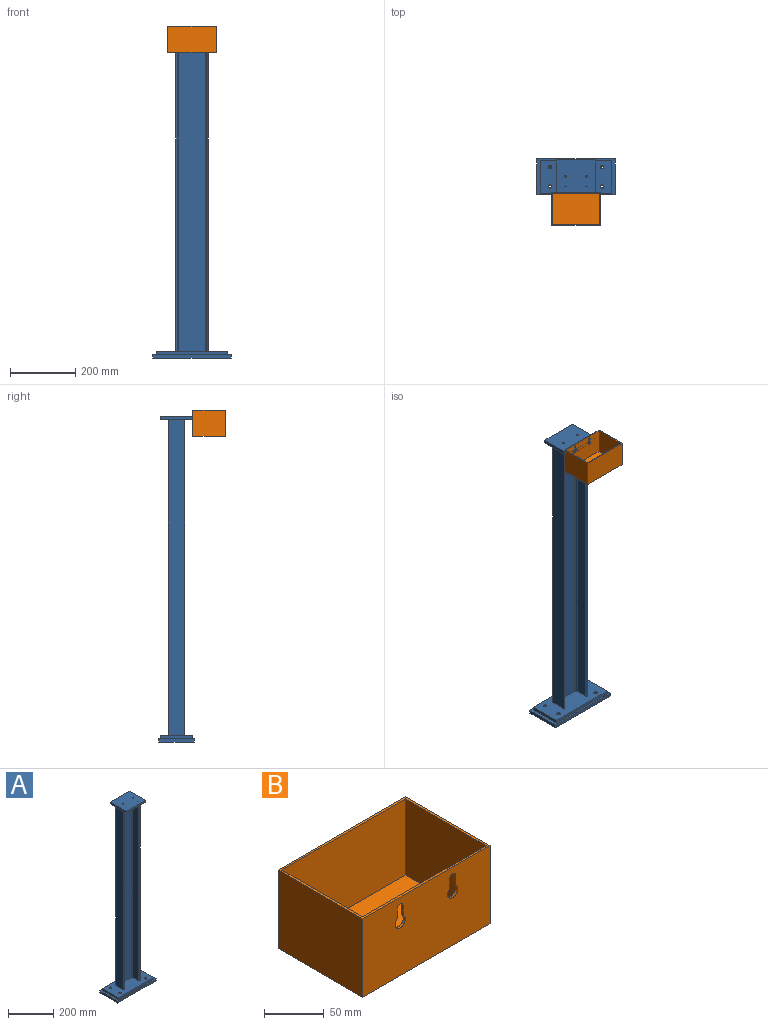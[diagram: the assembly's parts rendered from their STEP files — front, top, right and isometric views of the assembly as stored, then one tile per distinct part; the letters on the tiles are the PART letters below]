
ASSEMBLY  parts=2 mates=1
PART A: 45 faces, bbox 240x110x1000 mm
  f0: plane 220x100mm, normal (0,0,1), area 20669.9mm2, adj f15,f16,f17,f18,f19,f20,f21,f22
  f1: plane 11x11mm, normal (0,0,1), area 44.8mm2, adj f13,f21
  f2: plane 11x11mm, normal (0,0,1), area 44.8mm2, adj f9,f20
  f3: plane 11x11mm, normal (0,0,1), area 44.8mm2, adj f10,f19
  f4: plane 11x11mm, normal (0,0,1), area 44.8mm2, adj f11,f18
  f5: plane 240x110mm, normal (0,0,1), area 4400mm2, adj f6,f7,f8,f12,f15,f16,f17,f22
  f6: plane 110x10mm, normal (1,0,0), area 1100mm2, adj f5,f7,f12,f14
  f7: plane 240x10mm, normal (0,1,0), area 2400mm2, adj f5,f6,f8,f14
  f8: plane 110x10mm, normal (-1,0,0), area 1100mm2, adj f5,f7,f12,f14
  f9: cylinder r=4mm len=10mm, axis (0,0,1), area 251.3mm2, adj f2,f14
  f10: cylinder r=4mm len=10mm, axis (0,0,1), area 251.3mm2, adj f3,f14
  f11: cylinder r=4mm len=10mm, axis (0,0,1), area 251.3mm2, adj f4,f14
  f12: plane 240x10mm, normal (0,-1,0), area 2400mm2, adj f5,f6,f8,f14
  f13: cylinder r=4mm len=10mm, axis (0,0,1), area 251.3mm2, adj f1,f14
  f14: plane 240x110mm, normal (0,0,-1), area 26198.9mm2, adj f6,f7,f8,f9,f10,f11,f12,f13
  f15: plane 220x10mm, normal (0,1,0), area 2200mm2, adj f0,f5,f16,f22
  f16: plane 100x10mm, normal (-1,0,0), area 1000mm2, adj f0,f5,f15,f17
  f17: plane 220x10mm, normal (0,-1,0), area 2200mm2, adj f0,f5,f16,f22
  f18: cylinder r=5.5mm len=11mm, axis (0,0,-1), area 345.6mm2, adj f0,f4
  f19: cylinder r=5.5mm len=11mm, axis (0,0,-1), area 345.6mm2, adj f0,f3
  f20: cylinder r=5.5mm len=11mm, axis (0,0,-1), area 345.6mm2, adj f0,f2
  f21: cylinder r=5.5mm len=11mm, axis (0,0,-1), area 345.6mm2, adj f0,f1
  f22: plane 100x10mm, normal (1,0,0), area 1000mm2, adj f0,f5,f15,f17
  f23: plane 970x50mm, normal (1,0,0), area 48500mm2, adj f0,f24,f32,f33
  f24: plane 970x100mm, normal (0,1,0), area 97000mm2, adj f0,f23,f25,f33
  f25: plane 970x50mm, normal (-1,0,0), area 48500mm2, adj f0,f24,f26,f33
  f26: cylinder r=5mm len=970mm, axis (0,0,-1), area 7618.4mm2, adj f0,f25,f27,f33
  f27: plane 970x35mm, normal (1,0,0), area 33950mm2, adj f0,f26,f28,f33
  f28: cylinder r=5mm len=970mm, axis (0,0,-1), area 7618.4mm2, adj f0,f27,f29,f33
  f29: plane 970x80mm, normal (0,-1,0), area 77600mm2, adj f0,f28,f30,f33
  f30: cylinder r=5mm len=970mm, axis (0,0,-1), area 7618.4mm2, adj f0,f29,f31,f33
  f31: plane 970x35mm, normal (-1,0,0), area 33950mm2, adj f0,f30,f32,f33
  f32: cylinder r=5mm len=970mm, axis (0,0,-1), area 7618.4mm2, adj f0,f23,f31,f33
  f33: plane 120x100mm, normal (0,0,-1), area 10993.5mm2, adj f23,f24,f25,f26,f27,f28,f29,f30
  f34: plane 120x10mm, normal (0,1,0), area 1200mm2, adj f33,f35,f39,f40
  f35: plane 100x10mm, normal (-1,0,0), area 1000mm2, adj f33,f34,f36,f40
  f36: plane 120x10mm, normal (0,-1,0), area 1143.5mm2, adj f33,f35,f39,f40,f41,f43
  f37: cylinder r=3mm len=10mm, axis (0,0,-1), area 188.5mm2, adj f33,f40
  f38: cylinder r=3mm len=10mm, axis (0,0,-1), area 188.5mm2, adj f33,f40
  f39: plane 100x10mm, normal (1,0,0), area 1000mm2, adj f33,f34,f36,f40
  f40: plane 120x100mm, normal (0,0,1), area 11943.5mm2, adj f34,f35,f36,f37,f38,f39
  f41: cylinder r=3mm len=20mm, axis (0,-1,0), area 377mm2, adj f36,f42
  f42: plane 6x6mm, normal (0,-1,0), area 28.3mm2, adj f41
  f43: cylinder r=3mm len=20mm, axis (0,-1,0), area 377mm2, adj f36,f44
  f44: plane 6x6mm, normal (0,-1,0), area 28.3mm2, adj f43
PART B: 19 faces, bbox 150x100x80 mm
  f0: plane 150x80mm, normal (0,1,0), area 12000mm2, adj f1,f7,f8,f9
  f1: plane 100x80mm, normal (-1,0,0), area 8000mm2, adj f0,f2,f8,f9
  f2: plane 150x80mm, normal (0,-1,0), area 11604.3mm2, adj f1,f7,f8,f9,f10,f11,f12,f13
  f3: plane 95.4x77.7mm, normal (1,0,0), area 7412.6mm2, adj f4,f6,f8,f18
  f4: plane 145.4x77.7mm, normal (0,-1,0), area 11297.6mm2, adj f3,f5,f8,f18
  f5: plane 95.4x77.7mm, normal (-1,0,0), area 7412.6mm2, adj f4,f6,f8,f18
  f6: plane 145.4x77.7mm, normal (0,1,0), area 10901.9mm2, adj f3,f5,f8,f10,f11,f12,f13,f14
  f7: plane 100x80mm, normal (1,0,0), area 8000mm2, adj f0,f2,f8,f9
  f8: plane 150x100mm, normal (0,0,1), area 1128.8mm2, adj f0,f1,f2,f3,f4,f5,f6,f7
  f9: plane 150x100mm, normal (0,0,-1), area 15000mm2, adj f0,f1,f2,f7
  f10: cylinder r=3.5mm len=7mm, axis (0,-1,0), area 25.3mm2, adj f2,f6,f11,f13
  f11: plane 10.13x2.3mm, normal (1,0,0), area 23.3mm2, adj f2,f6,f10,f12
  f12: cylinder r=6mm len=12mm, axis (0,-1,0), area 69.5mm2, adj f2,f6,f11,f13
  f13: plane 10.13x2.3mm, normal (-1,0,0), area 23.3mm2, adj f2,f6,f10,f12
  f14: cylinder r=3.5mm len=7mm, axis (0,-1,0), area 25.3mm2, adj f2,f6,f15,f17
  f15: plane 10.13x2.3mm, normal (1,0,0), area 23.3mm2, adj f2,f6,f14,f16
  f16: cylinder r=6mm len=12mm, axis (0,-1,0), area 69.5mm2, adj f2,f6,f15,f17
  f17: plane 10.13x2.3mm, normal (-1,0,0), area 23.3mm2, adj f2,f6,f14,f16
  f18: plane 145.4x95.4mm, normal (0,0,1), area 13871.2mm2, adj f3,f4,f5,f6
PLACE A t=(0,0,10)mm fixed
PLACE B rot(axis=(0,0,1),180deg) t=(0,-100,940)mm
MATE revolute A.f43 <-> B.f12  axis (0,-1,0) through (-31,-50,995)mm
